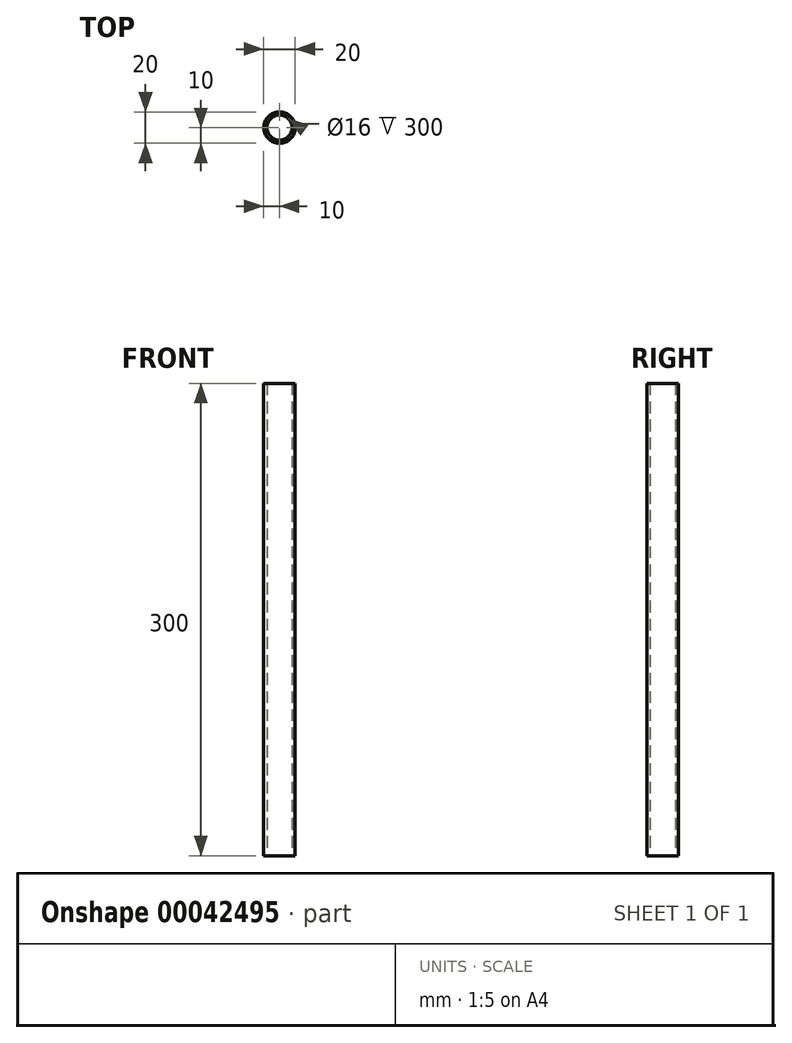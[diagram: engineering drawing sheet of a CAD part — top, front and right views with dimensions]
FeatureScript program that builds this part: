
annotation { "Feature Type Name" : "Feature", "Feature Type Description" : "" }
export const myFeature = defineFeature(function(context is Context, id is Id, definition is map)
    precondition{}
    {
        {
            var Q0;
            Q0=qCreatedBy(makeId("Top.planeOp"),FACE);
            var sketch = newSketch(context, id + "F0", { "sketchPlane" : qUnion([Q0])});
            skCircle(sketch, "E0", {"center": v(0, 0) * mm, "radius": 10 * mm});
            skCircle(sketch, "E1", {"center": v(0, 0) * mm, "radius": 8 * mm});
            skSolve(sketch);
        }
        {
            var Q0;
            Q0 = qSketchRegion(id + "F0", true);
            extrude(context, id + "F1", {"entities" : qUnion([Q0]), "depth" : 300 * mm});
        }
    });
